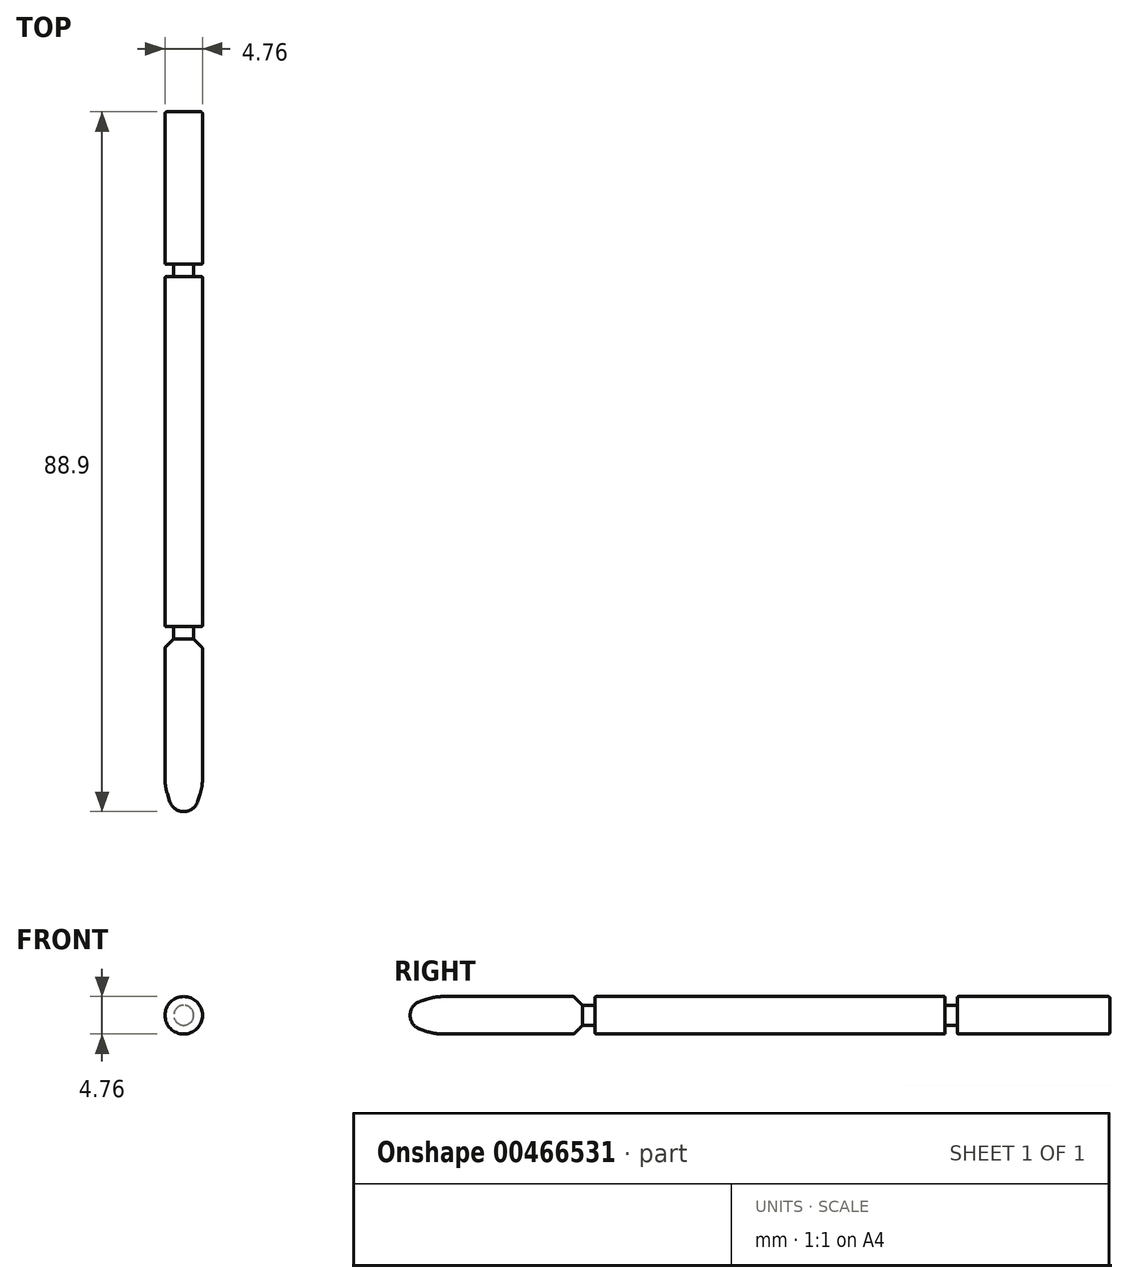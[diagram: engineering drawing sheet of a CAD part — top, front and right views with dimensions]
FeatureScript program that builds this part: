
annotation { "Feature Type Name" : "Feature", "Feature Type Description" : "" }
export const myFeature = defineFeature(function(context is Context, id is Id, definition is map)
    precondition{}
    {
        {
            var Q0;
            Q0=qCreatedBy(makeId("Front.planeOp"),FACE);
            var sketch = newSketch(context, id + "F0", { "sketchPlane" : qUnion([Q0])});
            skCircle(sketch, "E0", {"center": v(0, 0) * mm, "radius": 2.38 * mm});
            skSolve(sketch);
        }
        {
            var Q0;
            Q0 = qSketchRegion(id + "F0", true);
            extrude(context, id + "F1", {"entities" : qUnion([Q0]), "depth" : 88.9 * mm});
        }
        {
            var Q0;
            Q0=makeQuery(id+"F1.opExtrude","CAP_EDGE",EDGE,{"disambiguationData":[OSD([sQuery(id+"F0.wireOp",EDGE,"E0")])],"isStart":false});
            chamfer(context, id + "F2", {"entities" : qUnion([Q0]), "chamferType" : ChamferType.TWO_OFFSETS, "width1" : 1.02 * mm, "oppositeDirection" : false, "width2" : 3.17 * mm, "tangentPropagation" : true});
        }
        {
            var Q0;
            {var subQ0=sQuery(id+"F0.wireOp",EDGE,"E0");Q0=makeQuery(id+"F2.opChamfer","BLEND_EDGE",EDGE,{"blendedFrom":[makeQuery(id+"F1.opExtrude","CAP_EDGE",EDGE,{"disambiguationData":[OSD([subQ0])],"isStart":false}),makeQuery(id+"F1.opExtrude","CAP_FACE",FACE,{"disambiguationData":[OSD([subQ0])],"isStart":false})],"blendedInto":[makeQuery(id+"F1.opExtrude","CAP_FACE",FACE,{"disambiguationData":[OSD([subQ0])],"isStart":false})]});}
            fillet(context, id + "F3", {"entities" : qUnion([Q0]), "radius" : 1.85 * mm, "tangentPropagation" : true, "allowEdgeOverflow" : false});
        }
        {
            var Q0;
            {var subQ0=sQuery(id+"F0.wireOp",EDGE,"E0");Q0=makeQuery(id+"F2.opChamfer","BLEND_EDGE",EDGE,{"blendedFrom":[makeQuery(id+"F1.opExtrude","CAP_EDGE",EDGE,{"disambiguationData":[OSD([subQ0])],"isStart":false}),makeQuery(id+"F1.opExtrude","SWEPT_FACE",FACE,{"disambiguationData":[OSD([subQ0])]})],"blendedInto":[makeQuery(id+"F1.opExtrude","SWEPT_FACE",FACE,{"disambiguationData":[OSD([subQ0])]})]});}
            fillet(context, id + "F4", {"entities" : qUnion([Q0]), "radius" : 6.35 * mm, "tangentPropagation" : true, "allowEdgeOverflow" : false});
        }
        {
            var Q0;
            Q0=makeQuery(id+"F1.opExtrude","CAP_EDGE",EDGE,{"disambiguationData":[OSD([sQuery(id+"F0.wireOp",EDGE,"E0")])],"isStart":true});
            fillet(context, id + "F5", {"entities" : qUnion([Q0]), "radius" : 0.25 * mm, "tangentPropagation" : true, "allowEdgeOverflow" : false});
        }
        {
            var Q0;
            Q0=qCreatedBy(makeId("Top.planeOp"),FACE);
            var sketch = newSketch(context, id + "F6", { "sketchPlane" : qUnion([Q0])});
            skLineSegment(sketch, "E1.bottom", {"start": v(4.8, -19.37) * mm, "end": v(1.27, -19.37) * mm});
            skLineSegment(sketch, "E1.top", {"start": v(4.8, -20.96) * mm, "end": v(1.27, -20.96) * mm});
            skLineSegment(sketch, "E1.left", {"start": v(4.8, -19.37) * mm, "end": v(4.8, -20.95) * mm});
            skLineSegment(sketch, "E1.right", {"start": v(1.27, -19.37) * mm, "end": v(1.27, -20.96) * mm});
            skLineSegment(sketch, "E2", {"start": v(0, 0) * mm, "end": v(0, -23.6) * mm, "construction": true});
            skLineSegment(sketch, "E3.bottom", {"start": v(4.8, -67) * mm, "end": v(1.27, -67) * mm});
            skLineSegment(sketch, "E3.top", {"start": v(4.8, -65.4) * mm, "end": v(1.27, -65.4) * mm});
            skLineSegment(sketch, "E3.left", {"start": v(4.8, -67) * mm, "end": v(4.8, -65.4) * mm});
            skLineSegment(sketch, "E3.right", {"start": v(1.27, -67) * mm, "end": v(1.27, -65.4) * mm});
            skSolve(sketch);
        }
        {
            var Q0;
            Q0=makeQuery(id+"F6.imprint","IMPRINT",FACE,{"disambiguationData":[TD([[makeQuery(id+"F6.imprint","IMPRINT",EDGE,{"derivedFrom":sQuery(id+"F6.wireOp",EDGE,"E1.bottom")}),1.0]])]});
            var Q1;
            Q1=makeQuery(id+"F6.imprint","IMPRINT",FACE,{"disambiguationData":[TD([[makeQuery(id+"F6.imprint","IMPRINT",EDGE,{"derivedFrom":sQuery(id+"F6.wireOp",EDGE,"E3.bottom")}),-1.0]])]});
            var Q2;
            Q2=sQuery(id+"F6.wireOp",EDGE,"E1.bottom");
            var Q3;
            Q3=sQuery(id+"F6.wireOp",EDGE,"E1.left");
            var Q4;
            Q4=sQuery(id+"F6.wireOp",EDGE,"E1.top");
            var Q5;
            Q5=sQuery(id+"F6.wireOp",EDGE,"E1.right");
            var Q6;
            Q6=sQuery(id+"F6.wireOp",EDGE,"E2");
            revolve(context, id + "F7", {"operationType" : NewBodyOperationType.REMOVE, "entities" : qUnion([Q0, Q1]), "surfaceEntities" : qUnion([Q2, Q3, Q4, Q5]), "axis" : qUnion([Q6]), "revolveType" : RevolveType.FULL});
        }
        {
            var Q0;
            Q0=makeQuery(id+"F7.boolean.opBoolean","INTERSECT",EDGE,{"derivedFrom":[makeQuery(id+"F1.opExtrude","SWEPT_FACE",FACE,{"disambiguationData":[OSD([sQuery(id+"F0.wireOp",EDGE,"E0")])]}),makeQuery(id+"F7.opRevolve","SWEPT_FACE",FACE,{"disambiguationData":[OSD([sQuery(id+"F6.wireOp",EDGE,"E3.bottom")])]})]});
            chamfer(context, id + "F8", {"entities" : qUnion([Q0]), "width" : 1.12 * mm, "tangentPropagation" : true});
        }
        {
            var Q0;
            Q0=makeQuery(id+"F7.boolean.opBoolean","INTERSECT",EDGE,{"derivedFrom":[makeQuery(id+"F1.opExtrude","SWEPT_FACE",FACE,{"disambiguationData":[OSD([sQuery(id+"F0.wireOp",EDGE,"E0")])]}),makeQuery(id+"F7.opRevolve","SWEPT_FACE",FACE,{"disambiguationData":[OSD([sQuery(id+"F6.wireOp",EDGE,"E1.bottom")])]})]});
            var Q1;
            Q1=makeQuery(id+"F7.boolean.opBoolean","INTERSECT",EDGE,{"derivedFrom":[makeQuery(id+"F1.opExtrude","SWEPT_FACE",FACE,{"disambiguationData":[OSD([sQuery(id+"F0.wireOp",EDGE,"E0")])]}),makeQuery(id+"F7.opRevolve","SWEPT_FACE",FACE,{"disambiguationData":[OSD([sQuery(id+"F6.wireOp",EDGE,"E1.top")])]})]});
            var Q2;
            Q2=makeQuery(id+"F7.boolean.opBoolean","INTERSECT",EDGE,{"derivedFrom":[makeQuery(id+"F1.opExtrude","SWEPT_FACE",FACE,{"disambiguationData":[OSD([sQuery(id+"F0.wireOp",EDGE,"E0")])]}),makeQuery(id+"F7.opRevolve","SWEPT_FACE",FACE,{"disambiguationData":[OSD([sQuery(id+"F6.wireOp",EDGE,"E3.top")])]})]});
            var Q3;
            {var subQ0=sQuery(id+"F0.wireOp",EDGE,"E0");var subQ1=makeQuery(id+"F7.opRevolve","SWEPT_FACE",FACE,{"disambiguationData":[OSD([sQuery(id+"F6.wireOp",EDGE,"E3.bottom")])]});var subQ2=makeQuery(id+"F1.opExtrude","SWEPT_FACE",FACE,{"disambiguationData":[OSD([subQ0])]});Q3=makeQuery(id+"F8.opChamfer","BLEND_EDGE",EDGE,{"blendedFrom":[makeQuery(id+"F7.boolean.opBoolean","INTERSECT",EDGE,{"derivedFrom":[subQ2,subQ1]}),makeQuery(id+"F7.boolean.opBoolean","SPLIT",FACE,{"disambiguationData":[TD([makeQuery(id+"F4.opFillet","BLEND_FACE",FACE,{"disambiguationData":[OSD([subQ0])]})])],"derivedFrom":subQ2})],"blendedInto":[makeQuery(id+"F7.boolean.opBoolean","SPLIT",FACE,{"disambiguationData":[TD([makeQuery(id+"F4.opFillet","BLEND_FACE",FACE,{"disambiguationData":[OSD([subQ0])]})])],"derivedFrom":subQ2})]});}
            fillet(context, id + "F9", {"entities" : qUnion([Q0, Q1, Q2, Q3]), "radius" : 0.13 * mm, "tangentPropagation" : true, "allowEdgeOverflow" : false});
        }
    });
